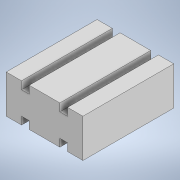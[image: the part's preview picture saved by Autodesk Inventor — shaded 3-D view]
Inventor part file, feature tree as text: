
AUTODESK INVENTOR PART (.ipt)
format: ipt  version: 2022 (Build 260153000, 153)  size: 121,344 bytes
history: native  units: mm
features: extrude x2, sketch x2, mirror x1
ambient origin geometry x8: Origin, YZ Plane, XZ Plane, XY Plane, X Axis, Y Axis, Z Axis, Center Point
bodies: Solid1 (feature_tree)
feature tree (5):
  extrude  "Extrusion1"  Depth=59.6mm
  extrude  "Extrusion2"  Depth=6.0mm
  mirror  "Mirror1"
  sketch  "Sketch1"  dims[d0=70.6mm d1=59.6mm]
  sketch  "Sketch2"  dims[d2=29.8mm d3=0.0mm d4=6.0mm d5=11.9mm d6=6.0mm d7=0.0mm]
